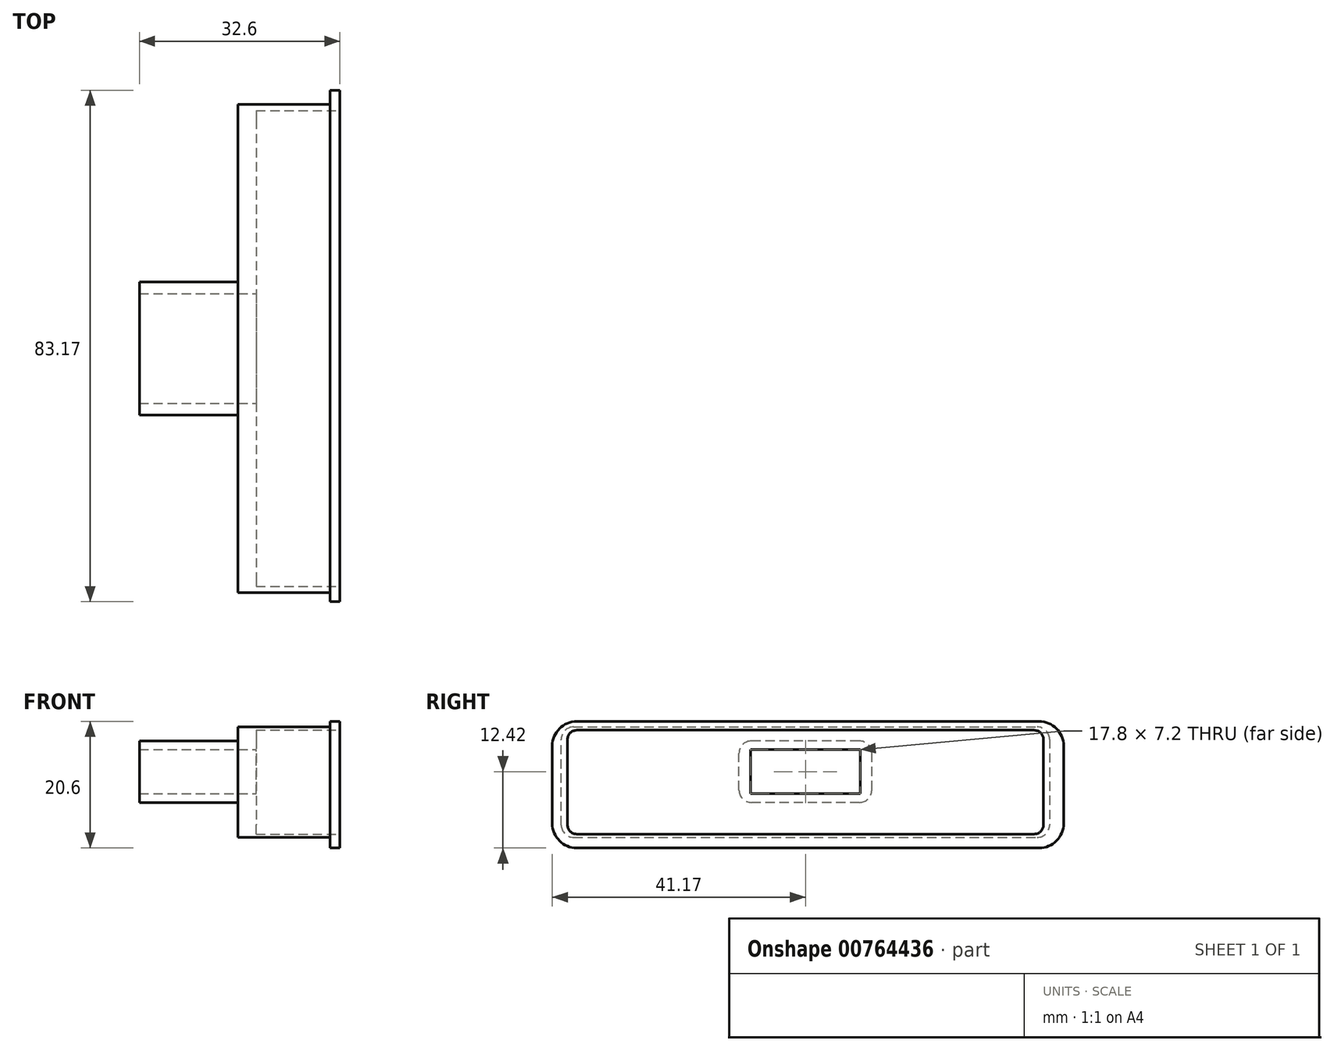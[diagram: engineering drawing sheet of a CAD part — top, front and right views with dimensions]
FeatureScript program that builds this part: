
annotation { "Feature Type Name" : "Feature", "Feature Type Description" : "" }
export const myFeature = defineFeature(function(context is Context, id is Id, definition is map)
    precondition{}
    {
        {
            var Q0;
            Q0=qCreatedBy(makeId("Right.planeOp"),FACE);
            var sketch = newSketch(context, id + "F0", { "sketchPlane" : qUnion([Q0])});
            skLineSegment(sketch, "E0.bottom", {"start": v(-37.17, -10.72) * mm, "end": v(38, -10.72) * mm});
            skLineSegment(sketch, "E0.top", {"start": v(-37.17, 9.88) * mm, "end": v(38, 9.88) * mm});
            skLineSegment(sketch, "E0.left", {"start": v(-41.17, -6.72) * mm, "end": v(-41.17, 5.88) * mm});
            skLineSegment(sketch, "E0.right", {"start": v(42, -6.72) * mm, "end": v(42, 5.88) * mm});
            skPoint(sketch, "E1.visualSharp", {"position": v(-41.17, 9.88) * mm});
            skArc(sketch, "E1.filletArc", {"start": v(-37.17, 9.88) * mm, "mid": v(-40, 8.71) * mm, "end": v(-41.17, 5.88) * mm});
            skPoint(sketch, "E2.visualSharp", {"position": v(-41.17, -10.72) * mm});
            skArc(sketch, "E2.filletArc", {"start": v(-41.17, -6.72) * mm, "mid": v(-40, -9.55) * mm, "end": v(-37.17, -10.72) * mm});
            skPoint(sketch, "E3.visualSharp", {"position": v(42, 9.88) * mm});
            skArc(sketch, "E3.filletArc", {"start": v(42, 5.88) * mm, "mid": v(40.83, 8.71) * mm, "end": v(38, 9.88) * mm});
            skPoint(sketch, "E4.visualSharp", {"position": v(42, -10.72) * mm});
            skArc(sketch, "E4.filletArc", {"start": v(38, -10.72) * mm, "mid": v(40.83, -9.55) * mm, "end": v(42, -6.72) * mm});
            skPoint(sketch, "E5.visualSharp", {"position": v(-36.41, 8.46) * mm});
            skPoint(sketch, "E6.visualSharp", {"position": v(-38.7, -8.45) * mm});
            skPoint(sketch, "E7.visualSharp", {"position": v(38.3, -8.15) * mm});
            skPoint(sketch, "E8.visualSharp", {"position": v(40.19, 8.46) * mm});
            skPoint(sketch, "E9.middle", {"position": v(0, 0) * mm});
            skLineSegment(sketch, "E10.bottom", {"start": v(-36.7, 8.98) * mm, "end": v(37.7, 8.98) * mm});
            skLineSegment(sketch, "E10.top", {"start": v(-37.78, -8.98) * mm, "end": v(37.7, -8.98) * mm});
            skLineSegment(sketch, "E10.left", {"start": v(-39.7, 5.98) * mm, "end": v(-39.7, -6.98) * mm});
            skLineSegment(sketch, "E10.right", {"start": v(39.7, 6.98) * mm, "end": v(39.7, -6.98) * mm});
            skPoint(sketch, "E11.visualSharp", {"position": v(-39.7, 8.98) * mm});
            skPoint(sketch, "E12.visualSharp", {"position": v(-39.7, -8.98) * mm});
            skPoint(sketch, "E13.visualSharp", {"position": v(39.7, -8.98) * mm});
            skPoint(sketch, "E14.visualSharp", {"position": v(39.7, 8.98) * mm});
            skPoint(sketch, "E15.visualSharp", {"position": v(10.8, 8.46) * mm});
            skPoint(sketch, "E16.visualSharp", {"position": v(-10.8, 8.46) * mm});
            skPoint(sketch, "E17.visualSharp", {"position": v(-10.8, -8.46) * mm});
            skPoint(sketch, "E18.visualSharp", {"position": v(10.8, -8.46) * mm});
            skPoint(sketch, "E19", {"position": v(0, 1.7) * mm});
            skLineSegment(sketch, "E20.bottom", {"start": v(8.9, -1.9) * mm, "end": v(-8.9, -1.9) * mm});
            skLineSegment(sketch, "E20.top", {"start": v(8.9, 5.3) * mm, "end": v(-8.9, 5.3) * mm});
            skLineSegment(sketch, "E20.left", {"start": v(8.9, -1.9) * mm, "end": v(8.9, 5.3) * mm});
            skLineSegment(sketch, "E20.right", {"start": v(-8.9, -1.9) * mm, "end": v(-8.9, 5.3) * mm});
            skLineSegment(sketch, "E21.bottom", {"start": v(8.8, -3.3) * mm, "end": v(-8.8, -3.3) * mm});
            skLineSegment(sketch, "E21.top", {"start": v(8.8, 6.7) * mm, "end": v(-8.8, 6.7) * mm});
            skLineSegment(sketch, "E21.left", {"start": v(10.8, -1.3) * mm, "end": v(10.8, 4.7) * mm});
            skLineSegment(sketch, "E21.right", {"start": v(-10.8, -1.3) * mm, "end": v(-10.8, 4.7) * mm});
            skPoint(sketch, "E22.visualSharp", {"position": v(10.8, -3.3) * mm});
            skArc(sketch, "E22.filletArc", {"start": v(8.8, -3.3) * mm, "mid": v(10.21, -2.71) * mm, "end": v(10.8, -1.3) * mm});
            skPoint(sketch, "E23.visualSharp", {"position": v(-10.8, -3.3) * mm});
            skArc(sketch, "E23.filletArc", {"start": v(-10.8, -1.3) * mm, "mid": v(-10.21, -2.71) * mm, "end": v(-8.8, -3.3) * mm});
            skPoint(sketch, "E24.visualSharp", {"position": v(-10.8, 6.7) * mm});
            skArc(sketch, "E24.filletArc", {"start": v(-8.8, 6.7) * mm, "mid": v(-10.21, 6.11) * mm, "end": v(-10.8, 4.7) * mm});
            skPoint(sketch, "E25.visualSharp", {"position": v(10.8, 6.7) * mm});
            skArc(sketch, "E25.filletArc", {"start": v(10.8, 4.7) * mm, "mid": v(10.21, 6.11) * mm, "end": v(8.8, 6.7) * mm});
            skLineSegment(sketch, "E26.bottom", {"start": v(-37.2, -8.45) * mm, "end": v(37.2, -8.45) * mm});
            skLineSegment(sketch, "E26.top", {"start": v(-37.2, 8.45) * mm, "end": v(37.2, 8.45) * mm});
            skLineSegment(sketch, "E26.left", {"start": v(-38.7, -6.95) * mm, "end": v(-38.7, 6.95) * mm});
            skLineSegment(sketch, "E26.right", {"start": v(38.7, -6.95) * mm, "end": v(38.7, 6.95) * mm});
            skPoint(sketch, "E27.visualSharp", {"position": v(-38.7, 8.45) * mm});
            skArc(sketch, "E27.filletArc", {"start": v(-37.2, 8.45) * mm, "mid": v(-38.26, 8.01) * mm, "end": v(-38.7, 6.95) * mm});
            skArc(sketch, "E28.filletArc", {"start": v(-38.7, -6.95) * mm, "mid": v(-38.26, -8.01) * mm, "end": v(-37.2, -8.45) * mm});
            skPoint(sketch, "E29.visualSharp", {"position": v(38.7, 8.45) * mm});
            skArc(sketch, "E29.filletArc", {"start": v(38.7, 6.95) * mm, "mid": v(38.26, 8.01) * mm, "end": v(37.2, 8.45) * mm});
            skPoint(sketch, "E30.visualSharp", {"position": v(38.7, -8.45) * mm});
            skArc(sketch, "E30.filletArc", {"start": v(37.2, -8.45) * mm, "mid": v(38.26, -8.01) * mm, "end": v(38.7, -6.95) * mm});
            skArc(sketch, "E31.filletArc", {"start": v(37.7, -8.98) * mm, "mid": v(39.11, -8.4) * mm, "end": v(39.7, -6.98) * mm});
            skLineSegment(sketch, "E32", {"start": v(-37.7, -8.98) * mm, "end": v(-37.78, -8.98) * mm});
            skArc(sketch, "E33.filletArc", {"start": v(-39.7, -6.98) * mm, "mid": v(-39.11, -8.4) * mm, "end": v(-37.7, -8.98) * mm});
            skArc(sketch, "E34.filletArc", {"start": v(39.7, 6.98) * mm, "mid": v(39.11, 8.4) * mm, "end": v(37.7, 8.98) * mm});
            skLineSegment(sketch, "E35", {"start": v(-36.7, 8.98) * mm, "end": v(-37.7, 8.98) * mm});
            skLineSegment(sketch, "E36", {"start": v(-39.7, 5.98) * mm, "end": v(-39.7, 6.98) * mm});
            skArc(sketch, "E37.filletArc", {"start": v(-37.7, 8.98) * mm, "mid": v(-39.11, 8.4) * mm, "end": v(-39.7, 6.98) * mm});
            skSolve(sketch);
        }
        {
            var Q0;
            Q0=makeQuery(id+"F0.imprint","IMPRINT",FACE,{"disambiguationData":[TD([[makeQuery(id+"F0.imprint","IMPRINT",EDGE,{"derivedFrom":sQuery(id+"F0.wireOp",EDGE,"E10.bottom")}),-1.0]])]});
            extrude(context, id + "F1", {"entities" : qUnion([Q0]), "oppositeDirection" : true, "depth" : 13 * mm, "offsetDistance" : 25 * mm});
        }
        {
            var Q0;
            Q0=makeQuery(id+"F0.imprint","IMPRINT",FACE,{"disambiguationData":[TD([[makeQuery(id+"F0.imprint","IMPRINT",EDGE,{"derivedFrom":sQuery(id+"F0.wireOp",EDGE,"E10.bottom")}),-1.0]])]});
            var Q1;
            Q1=makeQuery(id+"F0.imprint","IMPRINT",FACE,{"disambiguationData":[TD([[makeQuery(id+"F0.imprint","IMPRINT",EDGE,{"derivedFrom":sQuery(id+"F0.wireOp",EDGE,"E0.bottom")}),1.0]])]});
            extrude(context, id + "F2", {"entities" : qUnion([Q0, Q1]), "operationType" : NewBodyOperationType.ADD, "depth" : 1.6 * mm, "offsetDistance" : 25 * mm});
        }
        {
            var Q0;
            Q0=makeQuery(id+"F0.imprint","IMPRINT",FACE,{"disambiguationData":[TD([[makeQuery(id+"F0.imprint","IMPRINT",EDGE,{"derivedFrom":sQuery(id+"F0.wireOp",EDGE,"E10.bottom")}),-1.0]])]});
            var Q1;
            Q1=makeQuery(id+"F0.imprint","IMPRINT",FACE,{"disambiguationData":[TD([[makeQuery(id+"F0.imprint","IMPRINT",EDGE,{"derivedFrom":sQuery(id+"F0.wireOp",EDGE,"E21.bottom")}),1.0]])]});
            extrude(context, id + "F3", {"entities" : qUnion([Q0, Q1]), "operationType" : NewBodyOperationType.ADD, "oppositeDirection" : true, "depth" : 15 * mm, "offsetDistance" : 25 * mm, "hasSecondDirection" : true, "secondDirectionOppositeDirection" : true, "secondDirectionDepth" : 12 * mm});
        }
        {
            var Q0;
            Q0=makeQuery(id+"F0.imprint","IMPRINT",FACE,{"disambiguationData":[TD([[makeQuery(id+"F0.imprint","IMPRINT",EDGE,{"derivedFrom":sQuery(id+"F0.wireOp",EDGE,"E20.bottom")}),1.0]])]});
            extrude(context, id + "F4", {"entities" : qUnion([Q0]), "operationType" : NewBodyOperationType.ADD, "oppositeDirection" : true, "depth" : 31 * mm, "offsetDistance" : 25 * mm, "hasSecondDirection" : true, "secondDirectionOppositeDirection" : true, "secondDirectionDepth" : 12 * mm});
        }
    });
